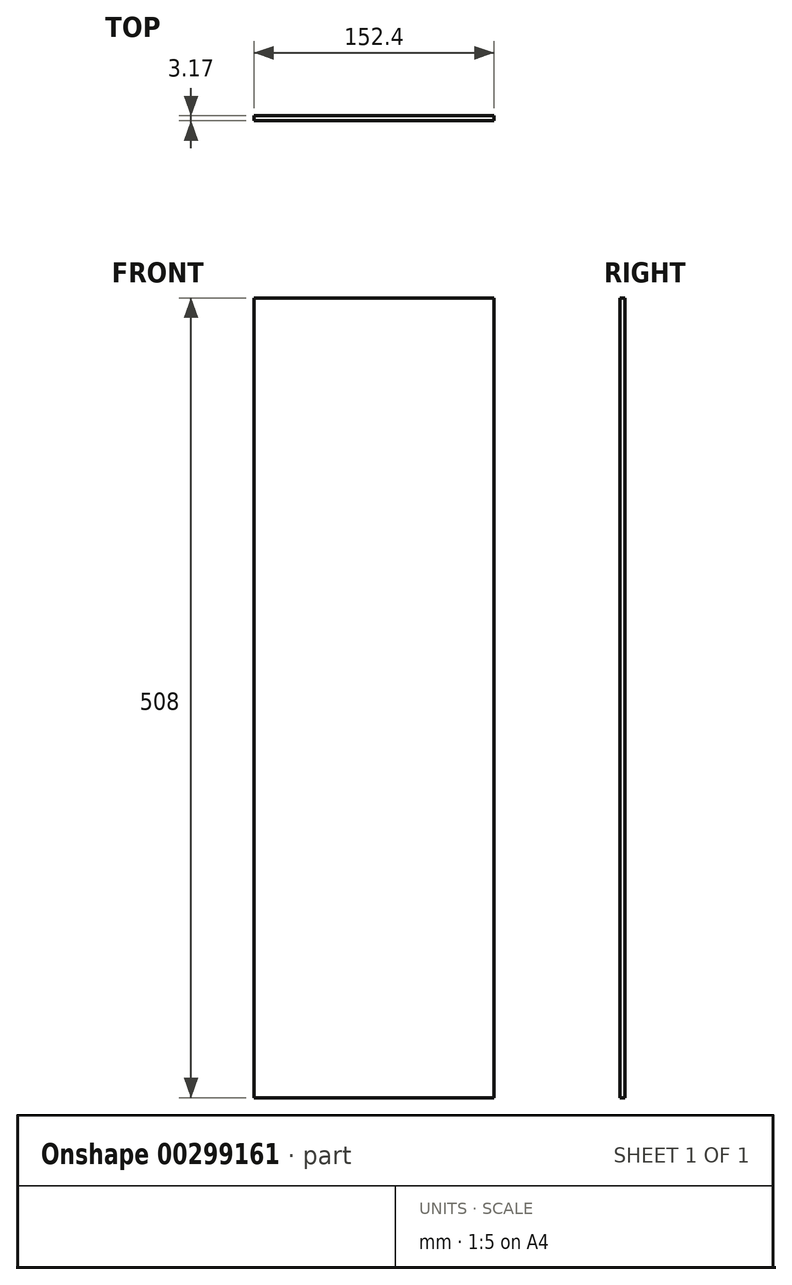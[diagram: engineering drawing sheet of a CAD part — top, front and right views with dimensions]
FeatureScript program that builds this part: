
annotation { "Feature Type Name" : "Feature", "Feature Type Description" : "" }
export const myFeature = defineFeature(function(context is Context, id is Id, definition is map)
    precondition{}
    {
        {
            var Q0;
            Q0=qCreatedBy(makeId("Front.planeOp"),FACE);
            var sketch = newSketch(context, id + "F0", { "sketchPlane" : qUnion([Q0])});
            skLineSegment(sketch, "E0.bottom", {"start": v(-76.2, 254) * mm, "end": v(76.2, 254) * mm});
            skLineSegment(sketch, "E0.top", {"start": v(-76.2, -254) * mm, "end": v(76.2, -254) * mm});
            skLineSegment(sketch, "E0.left", {"start": v(-76.2, 254) * mm, "end": v(-76.2, -254) * mm});
            skLineSegment(sketch, "E0.right", {"start": v(76.2, 254) * mm, "end": v(76.2, -254) * mm});
            skPoint(sketch, "E0.middle", {"position": v(0, 0) * mm});
            skSolve(sketch);
        }
        {
            var Q0;
            Q0 = qSketchRegion(id + "F0", true);
            extrude(context, id + "F1", {"entities" : qUnion([Q0]), "depth" : 3.17 * mm});
        }
    });
